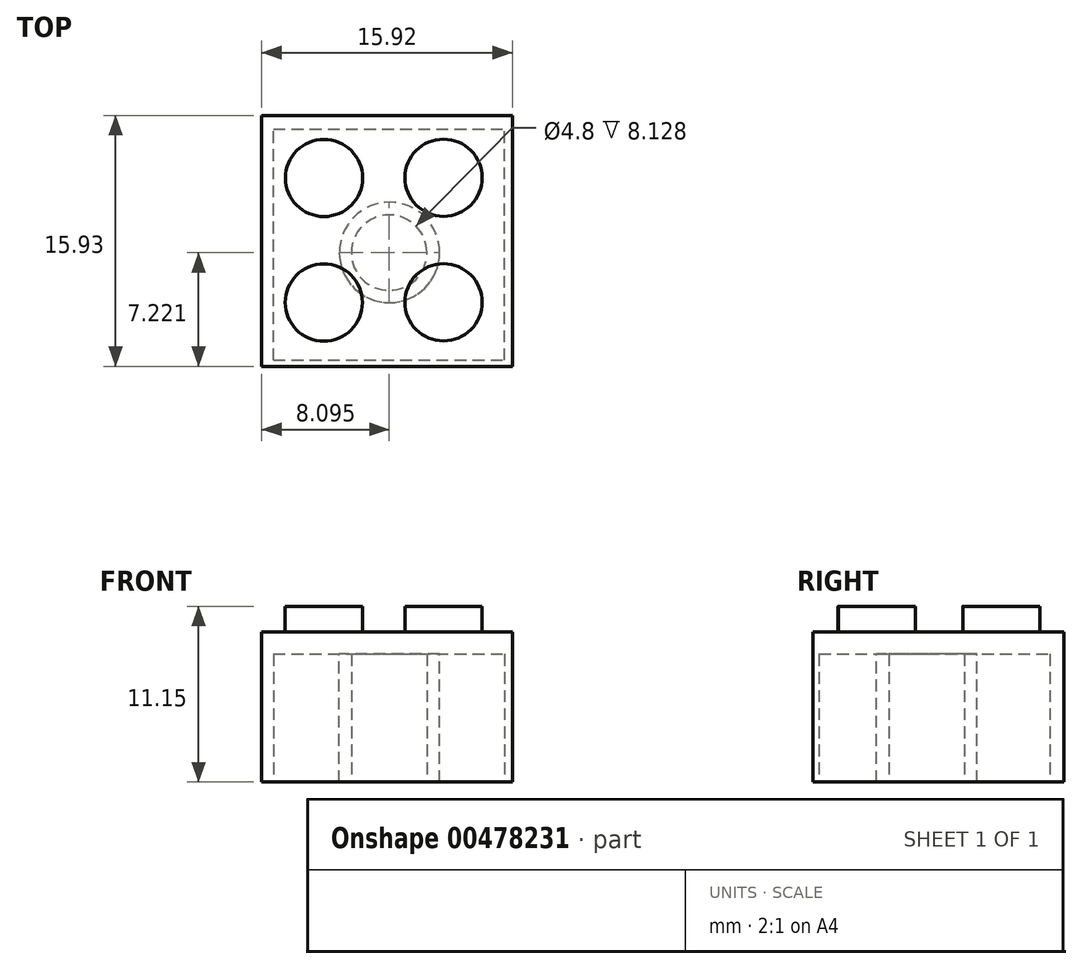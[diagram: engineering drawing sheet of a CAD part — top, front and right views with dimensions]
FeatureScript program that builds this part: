
annotation { "Feature Type Name" : "Feature", "Feature Type Description" : "" }
export const myFeature = defineFeature(function(context is Context, id is Id, definition is map)
    precondition{}
    {
        {
            var Q0;
            Q0=qCreatedBy(makeId("Top.planeOp"),FACE);
            var sketch = newSketch(context, id + "F0", { "sketchPlane" : qUnion([Q0])});
            skLineSegment(sketch, "E0.bottom", {"start": v(-11.55, 7.15) * mm, "end": v(4.37, 7.15) * mm});
            skLineSegment(sketch, "E0.top", {"start": v(-11.55, -8.78) * mm, "end": v(4.37, -8.78) * mm});
            skLineSegment(sketch, "E0.left", {"start": v(-11.55, 7.15) * mm, "end": v(-11.55, -8.78) * mm});
            skLineSegment(sketch, "E0.right", {"start": v(4.37, 7.15) * mm, "end": v(4.37, -8.78) * mm});
            skSolve(sketch);
        }
        {
            var Q0;
            Q0 = qSketchRegion(id + "F0", true);
            extrude(context, id + "F1", {"entities" : qUnion([Q0]), "depth" : 9.54 * mm, "offsetDistance" : 25.4 * mm});
        }
        {
            var Q0;
            Q0=makeQuery(id+"F1.opExtrude","CAP_FACE",FACE,{"disambiguationData":[OSD([sQuery(id+"F0.wireOp",EDGE,"E0.bottom"),sQuery(id+"F0.wireOp",EDGE,"E0.top"),sQuery(id+"F0.wireOp",EDGE,"E0.left"),sQuery(id+"F0.wireOp",EDGE,"E0.right")])],"isStart":false});
            var sketch = newSketch(context, id + "F2", { "sketchPlane" : qUnion([Q0])});
            skCircle(sketch, "E1", {"center": v(-7.59, 3.19) * mm, "radius": 2.45 * mm});
            skCircle(sketch, "E2", {"center": v(0, 3.2) * mm, "radius": 2.45 * mm});
            skCircle(sketch, "E3", {"center": v(-7.6, -4.73) * mm, "radius": 2.45 * mm});
            skCircle(sketch, "E4", {"center": v(0, -4.71) * mm, "radius": 2.45 * mm});
            skSolve(sketch);
        }
        {
            var Q0;
            Q0=makeQuery(id+"F2.imprint","IMPRINT",FACE,{"disambiguationData":[TD([[makeQuery(id+"F2.imprint","IMPRINT",EDGE,{"derivedFrom":sQuery(id+"F2.wireOp",EDGE,"E3")}),1.0]])]});
            extrude(context, id + "F3", {"entities" : qUnion([Q0]), "operationType" : NewBodyOperationType.ADD, "depth" : 1.61 * mm});
        }
        {
            var Q0;
            Q0=makeQuery(id+"F2.imprint","IMPRINT",FACE,{"disambiguationData":[TD([[makeQuery(id+"F2.imprint","IMPRINT",EDGE,{"derivedFrom":sQuery(id+"F2.wireOp",EDGE,"E4")}),1.0]])]});
            extrude(context, id + "F4", {"entities" : qUnion([Q0]), "operationType" : NewBodyOperationType.ADD, "depth" : 1.61 * mm});
        }
        {
            var Q0;
            Q0=makeQuery(id+"F2.imprint","IMPRINT",FACE,{"disambiguationData":[TD([[makeQuery(id+"F2.imprint","IMPRINT",EDGE,{"derivedFrom":sQuery(id+"F2.wireOp",EDGE,"E1")}),1.0]])]});
            extrude(context, id + "F5", {"entities" : qUnion([Q0]), "operationType" : NewBodyOperationType.ADD, "depth" : 1.61 * mm});
        }
        {
            var Q0;
            Q0=makeQuery(id+"F2.imprint","IMPRINT",FACE,{"disambiguationData":[TD([[makeQuery(id+"F2.imprint","IMPRINT",EDGE,{"derivedFrom":sQuery(id+"F2.wireOp",EDGE,"E2")}),1.0]])]});
            extrude(context, id + "F6", {"entities" : qUnion([Q0]), "operationType" : NewBodyOperationType.ADD, "depth" : 1.61 * mm});
        }
        {
            var Q0;
            Q0=makeQuery(id+"F1.opExtrude","CAP_FACE",FACE,{"disambiguationData":[OSD([sQuery(id+"F0.wireOp",EDGE,"E0.bottom"),sQuery(id+"F0.wireOp",EDGE,"E0.top"),sQuery(id+"F0.wireOp",EDGE,"E0.left"),sQuery(id+"F0.wireOp",EDGE,"E0.right")])],"isStart":true});
            var sketch = newSketch(context, id + "F7", { "sketchPlane" : qUnion([Q0])});
            skCircle(sketch, "E5", {"center": v(-3.5, 0.9) * mm, "radius": 3.18 * mm});
            skSolve(sketch);
        }
        {
            var Q0;
            Q0 = qSketchRegion(id + "F7", true);
            extrude(context, id + "F8", {"entities" : qUnion([Q0]), "operationType" : NewBodyOperationType.REMOVE, "oppositeDirection" : true, "depth" : 6.52 * mm});
        }
        {
            var Q0;
            Q0=makeQuery(id+"F0.imprint","IMPRINT",FACE,{"disambiguationData":[TD([[makeQuery(id+"F0.imprint","IMPRINT",EDGE,{"derivedFrom":sQuery(id+"F0.wireOp",EDGE,"E0.bottom")}),-1.0]])]});
            var sketch = newSketch(context, id + "F9", { "sketchPlane" : qUnion([Q0])});
            skLineSegment(sketch, "E6.bottom", {"start": v(-10.8, -8.4) * mm, "end": v(3.87, -8.4) * mm});
            skLineSegment(sketch, "E6.top", {"start": v(-10.8, 6.29) * mm, "end": v(3.87, 6.29) * mm});
            skLineSegment(sketch, "E6.left", {"start": v(-10.8, -8.4) * mm, "end": v(-10.8, 6.29) * mm});
            skLineSegment(sketch, "E6.right", {"start": v(3.87, -8.4) * mm, "end": v(3.87, 6.29) * mm});
            skSolve(sketch);
        }
        {
            var Q0;
            Q0=makeQuery(id+"F9.imprint","IMPRINT",FACE,{"disambiguationData":[TD([[makeQuery(id+"F9.imprint","IMPRINT",EDGE,{"derivedFrom":sQuery(id+"F9.wireOp",EDGE,"E6.bottom")}),1.0]])]});
            var Q1;
            Q1=sQuery(id+"F9.wireOp",EDGE,"E6.bottom");
            var Q2;
            Q2=sQuery(id+"F9.wireOp",EDGE,"E6.left");
            var Q3;
            Q3=sQuery(id+"F9.wireOp",EDGE,"E6.top");
            var Q4;
            Q4=sQuery(id+"F9.wireOp",EDGE,"E6.right");
            extrude(context, id + "F10", {"entities" : qUnion([Q0]), "operationType" : NewBodyOperationType.REMOVE, "surfaceEntities" : qUnion([Q1, Q2, Q3, Q4]), "depth" : 8.13 * mm});
        }
        {
            var Q0;
            Q0=qCreatedBy(makeId("Top.planeOp"),FACE);
            var sketch = newSketch(context, id + "F11", { "sketchPlane" : qUnion([Q0])});
            skCircle(sketch, "E7", {"center": v(-3.52, -0.85) * mm, "radius": 3.2 * mm});
            skSolve(sketch);
        }
        {
            var Q0;
            Q0=makeQuery(id+"F11.imprint","IMPRINT",FACE,{"disambiguationData":[TD([[makeQuery(id+"F11.imprint","IMPRINT",EDGE,{"derivedFrom":sQuery(id+"F11.wireOp",EDGE,"E7")}),1.0]])]});
            var Q1;
            Q1=sQuery(id+"F11.wireOp",EDGE,"E7");
            extrude(context, id + "F12", {"entities" : qUnion([Q0]), "operationType" : NewBodyOperationType.ADD, "surfaceEntities" : qUnion([Q1]), "depth" : 6.86 * mm});
        }
        {
            var Q0;
            Q0=makeQuery(id+"F12.opExtrude","CAP_FACE",FACE,{"disambiguationData":[OSD([sQuery(id+"F11.wireOp",EDGE,"E7")])],"isStart":true});
            var sketch = newSketch(context, id + "F13", { "sketchPlane" : qUnion([Q0])});
            skCircle(sketch, "E8", {"center": v(-3.53, 0.83) * mm, "radius": 2.46 * mm});
            skSolve(sketch);
        }
        {
            var Q0;
            Q0 = qSketchRegion(id + "F13", true);
            extrude(context, id + "F14", {"entities" : qUnion([Q0]), "operationType" : NewBodyOperationType.REMOVE, "oppositeDirection" : true, "depth" : 6.86 * mm});
        }
        {
            var Q0;
            Q0=makeQuery(id+"F12.opExtrude","SWEPT_BODY",BODY,{"disambiguationData":[OSD([sQuery(id+"F11.wireOp",EDGE,"E7")])]});
            deleteBodies(context, id + "F15", {"entities" : qUnion([Q0])});
        }
        {
            var Q0;
            Q0=makeQuery(id+"F10.boolean.opBoolean","COPY",FACE,{"derivedFrom":makeQuery(id+"F10.opExtrude","CAP_FACE",FACE,{"disambiguationData":[OSD([sQuery(id+"F9.wireOp",EDGE,"E6.bottom"),sQuery(id+"F9.wireOp",EDGE,"E6.top"),sQuery(id+"F9.wireOp",EDGE,"E6.left"),sQuery(id+"F9.wireOp",EDGE,"E6.right")])],"isStart":false})});
            var sketch = newSketch(context, id + "F16", { "sketchPlane" : qUnion([Q0])});
            skCircle(sketch, "E9", {"center": v(-3.43, 1.55) * mm, "radius": 3.19 * mm});
            skSolve(sketch);
        }
        {
            var Q0;
            Q0=makeQuery(id+"F16.imprint","IMPRINT",FACE,{"disambiguationData":[TD([[makeQuery(id+"F16.imprint","IMPRINT",EDGE,{"derivedFrom":sQuery(id+"F16.wireOp",EDGE,"E9")}),1.0]])]});
            extrude(context, id + "F17", {"entities" : qUnion([Q0]), "operationType" : NewBodyOperationType.ADD, "depth" : 8.13 * mm, "offsetDistance" : 25.4 * mm});
        }
        {
            var Q0;
            Q0=makeQuery(id+"F17.opExtrude","CAP_FACE",FACE,{"disambiguationData":[OSD([sQuery(id+"F16.wireOp",EDGE,"E9")])],"isStart":false});
            var sketch = newSketch(context, id + "F18", { "sketchPlane" : qUnion([Q0])});
            skCircle(sketch, "E10", {"center": v(-3.45, 1.56) * mm, "radius": 2.4 * mm});
            skSolve(sketch);
        }
        {
            var Q0;
            Q0 = qSketchRegion(id + "F18", true);
            extrude(context, id + "F19", {"entities" : qUnion([Q0]), "operationType" : NewBodyOperationType.REMOVE, "oppositeDirection" : true, "depth" : 8.13 * mm, "offsetDistance" : 25.4 * mm});
        }
    });
